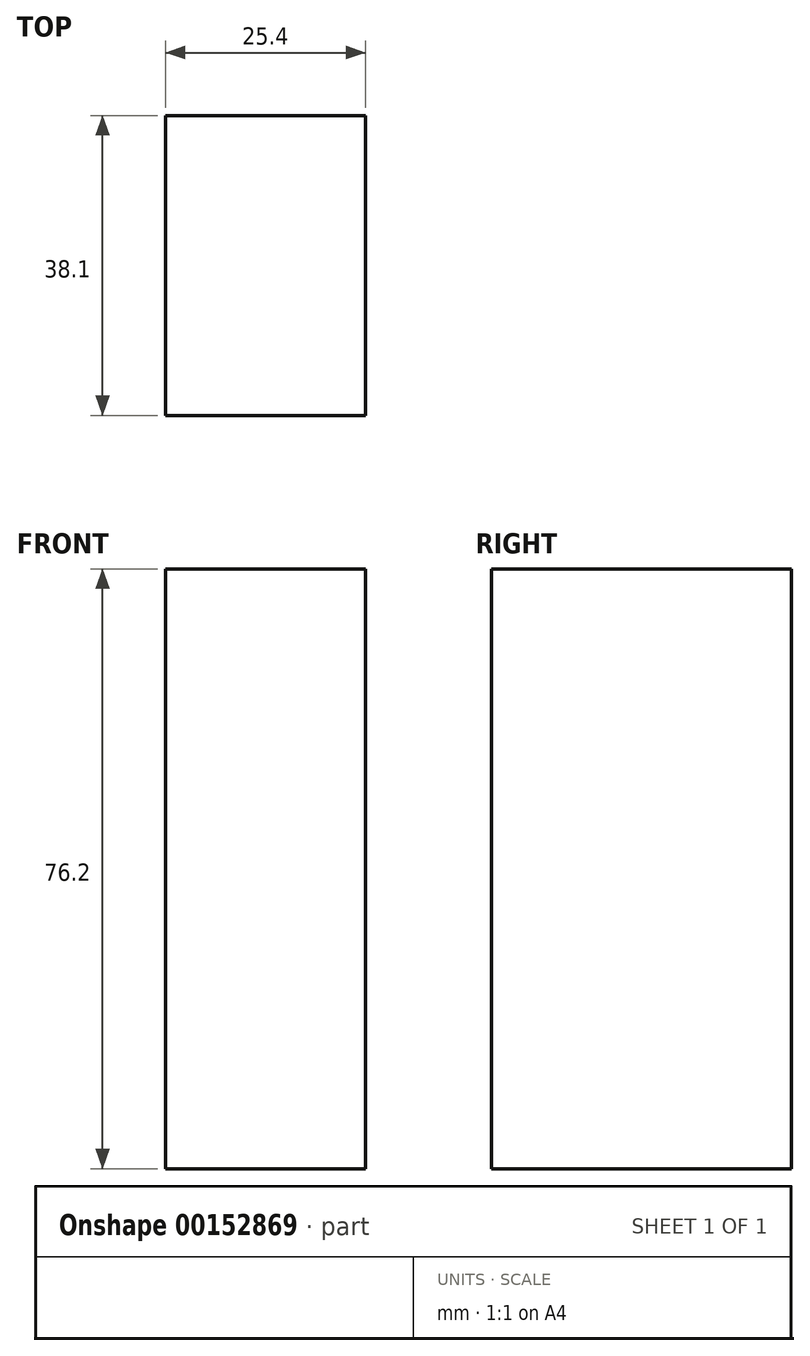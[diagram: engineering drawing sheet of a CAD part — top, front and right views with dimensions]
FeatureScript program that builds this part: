
annotation { "Feature Type Name" : "Feature", "Feature Type Description" : "" }
export const myFeature = defineFeature(function(context is Context, id is Id, definition is map)
    precondition{}
    {
        {
            var Q0;
            Q0=qCreatedBy(makeId("Top.planeOp"),FACE);
            var sketch = newSketch(context, id + "F0", { "sketchPlane" : qUnion([Q0])});
            skLineSegment(sketch, "E0.bottom", {"start": v(12.7, -19.05) * mm, "end": v(-12.7, -19.05) * mm});
            skLineSegment(sketch, "E0.top", {"start": v(12.7, 19.05) * mm, "end": v(-12.7, 19.05) * mm});
            skLineSegment(sketch, "E0.left", {"start": v(12.7, -19.05) * mm, "end": v(12.7, 19.05) * mm});
            skLineSegment(sketch, "E0.right", {"start": v(-12.7, -19.05) * mm, "end": v(-12.7, 19.05) * mm});
            skPoint(sketch, "E0.middle", {"position": v(0, 0) * mm});
            skSolve(sketch);
        }
        {
            var Q0;
            Q0=qSketchRegion(id+"F0",true);
            extrude(context, id + "F1", {"entities" : qUnion([Q0]), "depth" : 76.2 * mm});
        }
    });
